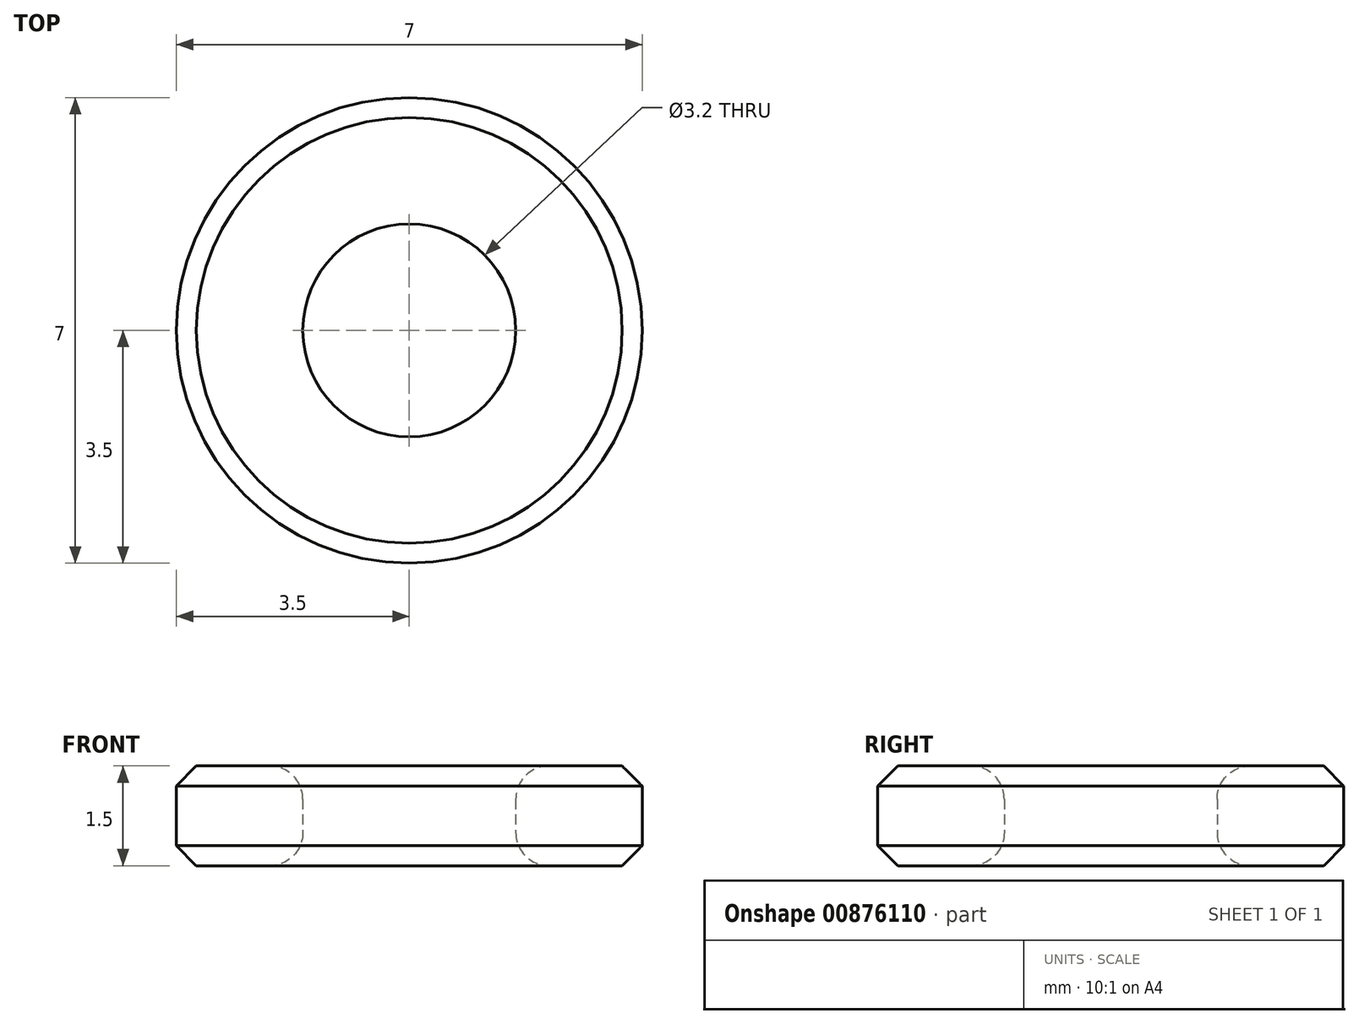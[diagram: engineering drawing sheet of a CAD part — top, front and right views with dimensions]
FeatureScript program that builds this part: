
annotation { "Feature Type Name" : "Feature", "Feature Type Description" : "" }
export const myFeature = defineFeature(function(context is Context, id is Id, definition is map)
    precondition{}
    {
        {
            var Q0;
            Q0=qCreatedBy(makeId("Top.planeOp"),FACE);
            var sketch = newSketch(context, id + "F0", { "sketchPlane" : qUnion([Q0])});
            skCircle(sketch, "E0", {"center": v(0, 0) * mm, "radius": 3.5 * mm});
            skCircle(sketch, "E1", {"center": v(0, 0) * mm, "radius": 1.6 * mm});
            skSolve(sketch);
        }
        {
            var Q0;
            Q0=makeQuery(id+"F0.imprint","IMPRINT",FACE,{"disambiguationData":[TD([[makeQuery(id+"F0.imprint","IMPRINT",EDGE,{"derivedFrom":sQuery(id+"F0.wireOp",EDGE,"E0")}),1.0]])]});
            extrude(context, id + "F1", {"entities" : qUnion([Q0]), "depth" : 1.5 * mm, "offsetDistance" : 25 * mm});
        }
        {
            var Q0;
            Q0=makeQuery(id+"F1.opExtrude","SWEPT_FACE",FACE,{"disambiguationData":[OSD([sQuery(id+"F0.wireOp",EDGE,"E1")])]});
            fillet(context, id + "F2", {"entities" : qUnion([Q0]), "radius" : .5 * mm, "tangentPropagation" : true, "allowEdgeOverflow" : false});
        }
        {
            var Q0;
            Q0=makeQuery(id+"F1.opExtrude","SWEPT_FACE",FACE,{"disambiguationData":[OSD([sQuery(id+"F0.wireOp",EDGE,"E0")])]});
            chamfer(context, id + "F3", {"entities" : qUnion([Q0]), "width" : .3 * mm, "tangentPropagation" : true});
        }
    });
